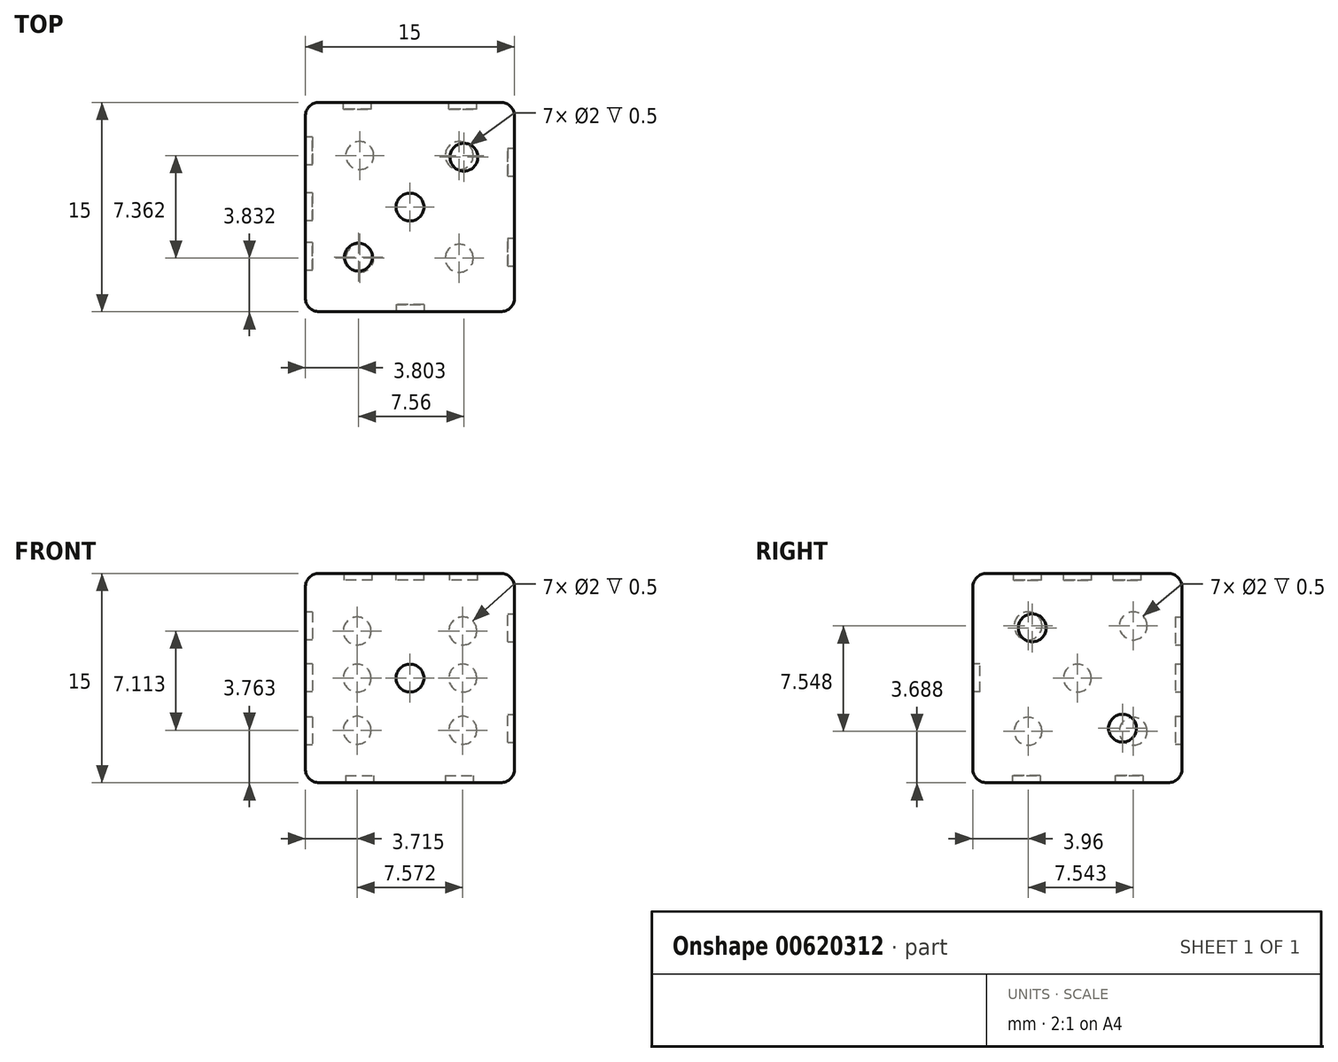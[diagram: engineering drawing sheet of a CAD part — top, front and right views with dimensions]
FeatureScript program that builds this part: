
annotation { "Feature Type Name" : "Feature", "Feature Type Description" : "" }
export const myFeature = defineFeature(function(context is Context, id is Id, definition is map)
    precondition{}
    {
        {
            var Q0;
            Q0=qCreatedBy(makeId("Front.planeOp"),FACE);
            var sketch = newSketch(context, id + "F0", { "sketchPlane" : qUnion([Q0])});
            skLineSegment(sketch, "E0.bottom", {"start": v(7.5, 7.5) * mm, "end": v(-7.5, 7.5) * mm});
            skLineSegment(sketch, "E0.top", {"start": v(7.5, -7.5) * mm, "end": v(-7.5, -7.5) * mm});
            skLineSegment(sketch, "E0.left", {"start": v(7.5, 7.5) * mm, "end": v(7.5, -7.5) * mm});
            skLineSegment(sketch, "E0.right", {"start": v(-7.5, 7.5) * mm, "end": v(-7.5, -7.5) * mm});
            skPoint(sketch, "E0.middle", {"position": v(0, 0) * mm});
            skSolve(sketch);
        }
        {
            var Q0;
            Q0 = qSketchRegion(id + "F0", true);
            extrude(context, id + "F1", {"entities" : qUnion([Q0]), "depth" : 15 * mm, "offsetDistance" : 25.4 * mm});
        }
        {
            var Q0;
            Q0=makeQuery(id+"F1.opExtrude","CAP_FACE",FACE,{"disambiguationData":[OSD([sQuery(id+"F0.wireOp",EDGE,"E0.bottom"),sQuery(id+"F0.wireOp",EDGE,"E0.top"),sQuery(id+"F0.wireOp",EDGE,"E0.left"),sQuery(id+"F0.wireOp",EDGE,"E0.right")])],"isStart":false});
            var sketch = newSketch(context, id + "F2", { "sketchPlane" : qUnion([Q0])});
            skCircle(sketch, "E1", {"center": v(0, 0) * mm, "radius": 1 * mm});
            skSolve(sketch);
        }
        {
            var Q0;
            Q0=makeQuery(id+"F1.opExtrude","CAP_FACE",FACE,{"disambiguationData":[OSD([sQuery(id+"F0.wireOp",EDGE,"E0.bottom"),sQuery(id+"F0.wireOp",EDGE,"E0.top"),sQuery(id+"F0.wireOp",EDGE,"E0.left"),sQuery(id+"F0.wireOp",EDGE,"E0.right")])],"isStart":true});
            var sketch = newSketch(context, id + "F3", { "sketchPlane" : qUnion([Q0])});
            skSolve(sketch);
        }
        {
            var Q0;
            Q0=makeQuery(id+"F2.imprint","IMPRINT",FACE,{"disambiguationData":[TD([[makeQuery(id+"F2.imprint","IMPRINT",EDGE,{"derivedFrom":sQuery(id+"F2.wireOp",EDGE,"E1")}),1.0]])]});
            extrude(context, id + "F4", {"entities" : qUnion([Q0]), "operationType" : NewBodyOperationType.REMOVE, "oppositeDirection" : true, "depth" : 0.5 * mm, "offsetDistance" : 25.4 * mm});
        }
        {
            var Q0;
            Q0=makeQuery(id+"F3.imprint","IMPRINT",FACE,{"disambiguationData":[TD([[makeQuery(id+"F3.imprint","IMPRINT",EDGE,{"derivedFrom":makeQuery(id+"F1.opExtrude","CAP_EDGE",EDGE,{"disambiguationData":[OSD([sQuery(id+"F0.wireOp",EDGE,"E0.bottom")])],"isStart":true})}),-1.0]])]});
            var sketch = newSketch(context, id + "F5", { "sketchPlane" : qUnion([Q0])});
            skLineSegment(sketch, "E2", {"start": v(0, 0) * mm, "end": v(0, -7.54) * mm});
            skPoint(sketch, "E3", {"position": v(-7.48, -3.74) * mm});
            skPoint(sketch, "E4", {"position": v(-3.79, -7.54) * mm});
            skPoint(sketch, "E5", {"position": v(3.79, -7.5) * mm});
            skPoint(sketch, "E6", {"position": v(7.42, -3.74) * mm});
            skPoint(sketch, "E7", {"position": v(-3.79, 7.52) * mm});
            skPoint(sketch, "E8", {"position": v(-7.48, 3.38) * mm});
            skPoint(sketch, "E9", {"position": v(0, 7.52) * mm});
            skPoint(sketch, "E10", {"position": v(3.84, 7.52) * mm});
            skPoint(sketch, "E11", {"position": v(7.31, 3.38) * mm});
            skCircle(sketch, "E12", {"center": v(3.79, -3.74) * mm, "radius": 1 * mm});
            skCircle(sketch, "E13", {"center": v(3.79, 0) * mm, "radius": 1 * mm});
            skCircle(sketch, "E14", {"center": v(3.79, 3.38) * mm, "radius": 1 * mm});
            skCircle(sketch, "E15", {"center": v(-3.79, -3.74) * mm, "radius": 1 * mm});
            skCircle(sketch, "E16", {"center": v(-3.79, 0) * mm, "radius": 1 * mm});
            skCircle(sketch, "E17", {"center": v(-3.79, 3.38) * mm, "radius": 1 * mm});
            skSolve(sketch);
        }
        {
            var Q0;
            Q0 = qSketchRegion(id + "F5", true);
            extrude(context, id + "F6", {"entities" : qUnion([Q0]), "operationType" : NewBodyOperationType.REMOVE, "oppositeDirection" : true, "depth" : 0.5 * mm, "offsetDistance" : 25.4 * mm});
        }
        {
            var Q0;
            Q0=makeQuery(id+"F1.opExtrude","SWEPT_FACE",FACE,{"disambiguationData":[OSD([sQuery(id+"F0.wireOp",EDGE,"E0.top")])]});
            var sketch = newSketch(context, id + "F7", { "sketchPlane" : qUnion([Q0])});
            skPoint(sketch, "E18", {"position": v(-3.6, 0) * mm});
            skPoint(sketch, "E19", {"position": v(-7.5, 7.5) * mm});
            skPoint(sketch, "E20", {"position": v(-7.5, 3.8) * mm});
            skPoint(sketch, "E21", {"position": v(-7.5, 11.17) * mm});
            skPoint(sketch, "E22", {"position": v(-3.6, 15) * mm});
            skPoint(sketch, "E23", {"position": v(7.5, 7.5) * mm});
            skPoint(sketch, "E24", {"position": v(3.53, 0) * mm});
            skPoint(sketch, "E25", {"position": v(7.5, 3.8) * mm});
            skPoint(sketch, "E26", {"position": v(7.5, 11.17) * mm});
            skCircle(sketch, "E27", {"center": v(3.53, 3.8) * mm, "radius": 1 * mm});
            skCircle(sketch, "E28", {"center": v(3.53, 11.17) * mm, "radius": 1 * mm});
            skCircle(sketch, "E29", {"center": v(-3.6, 3.8) * mm, "radius": 1 * mm});
            skCircle(sketch, "E30", {"center": v(-3.6, 11.17) * mm, "radius": 1 * mm});
            skSolve(sketch);
        }
        {
            var Q0;
            Q0 = qSketchRegion(id + "F7", true);
            extrude(context, id + "F8", {"entities" : qUnion([Q0]), "operationType" : NewBodyOperationType.REMOVE, "oppositeDirection" : true, "depth" : 0.5 * mm, "offsetDistance" : 25.4 * mm});
        }
        {
            var Q0;
            Q0=makeQuery(id+"F1.opExtrude","SWEPT_FACE",FACE,{"disambiguationData":[OSD([sQuery(id+"F0.wireOp",EDGE,"E0.right")])]});
            var sketch = newSketch(context, id + "F9", { "sketchPlane" : qUnion([Q0])});
            skPoint(sketch, "E31", {"position": v(0, 0) * mm});
            skPoint(sketch, "E32", {"position": v(3.5, 7.5) * mm});
            skPoint(sketch, "E33", {"position": v(11.04, 7.5) * mm});
            skPoint(sketch, "E34", {"position": v(11.04, -7.5) * mm});
            skPoint(sketch, "E35", {"position": v(3.5, -7.5) * mm});
            skPoint(sketch, "E35.positionSnap0", {"position": v(7.5, -7.5) * mm});
            skPoint(sketch, "E36", {"position": v(0, -3.81) * mm});
            skPoint(sketch, "E37", {"position": v(0, 3.74) * mm});
            skPoint(sketch, "E38", {"position": v(15, 3.74) * mm});
            skPoint(sketch, "E39", {"position": v(15, -3.81) * mm});
            skCircle(sketch, "E40", {"center": v(7.5, 0) * mm, "radius": 1 * mm});
            skCircle(sketch, "E41", {"center": v(3.5, -3.81) * mm, "radius": 1 * mm});
            skCircle(sketch, "E42", {"center": v(11.04, -3.81) * mm, "radius": 1 * mm});
            skCircle(sketch, "E43", {"center": v(11.04, 3.74) * mm, "radius": 1 * mm});
            skCircle(sketch, "E44", {"center": v(3.5, 3.74) * mm, "radius": 1 * mm});
            skSolve(sketch);
        }
        {
            var Q0;
            Q0 = qSketchRegion(id + "F9", true);
            extrude(context, id + "F10", {"entities" : qUnion([Q0]), "operationType" : NewBodyOperationType.REMOVE, "oppositeDirection" : true, "depth" : 0.5 * mm, "offsetDistance" : 25.4 * mm});
        }
        {
            var Q0;
            Q0=makeQuery(id+"F1.opExtrude","SWEPT_FACE",FACE,{"disambiguationData":[OSD([sQuery(id+"F0.wireOp",EDGE,"E0.left")])]});
            var sketch = newSketch(context, id + "F11", { "sketchPlane" : qUnion([Q0])});
            skPoint(sketch, "E45", {"position": v(0, -3.6) * mm});
            skPoint(sketch, "E46", {"position": v(-4.27, -7.5) * mm});
            skPoint(sketch, "E47", {"position": v(-10.73, -7.5) * mm});
            skPoint(sketch, "E48", {"position": v(0, 3.6) * mm});
            skCircle(sketch, "E49", {"center": v(-4.27, -3.6) * mm, "radius": 1 * mm});
            skCircle(sketch, "E50", {"center": v(-10.73, 3.6) * mm, "radius": 1 * mm});
            skSolve(sketch);
        }
        {
            var Q0;
            Q0 = qSketchRegion(id + "F11", true);
            extrude(context, id + "F12", {"entities" : qUnion([Q0]), "operationType" : NewBodyOperationType.REMOVE, "oppositeDirection" : true, "depth" : 0.5 * mm, "offsetDistance" : 25.4 * mm});
        }
        {
            var Q0;
            Q0=makeQuery(id+"F1.opExtrude","SWEPT_FACE",FACE,{"disambiguationData":[OSD([sQuery(id+"F0.wireOp",EDGE,"E0.bottom")])]});
            var sketch = newSketch(context, id + "F13", { "sketchPlane" : qUnion([Q0])});
            skPoint(sketch, "E51", {"position": v(3.86, 0) * mm});
            skPoint(sketch, "E52", {"position": v(7.5, -3.93) * mm});
            skPoint(sketch, "E53", {"position": v(-7.5, -11.09) * mm});
            skPoint(sketch, "E54", {"position": v(-3.7, -15) * mm});
            skCircle(sketch, "E55", {"center": v(3.86, -3.93) * mm, "radius": 1 * mm});
            skCircle(sketch, "E56", {"center": v(0, -7.5) * mm, "radius": 1 * mm});
            skPoint(sketch, "E56.centerSnap0", {"position": v(-7.5, -7.5) * mm});
            skCircle(sketch, "E57", {"center": v(-3.7, -11.09) * mm, "radius": 1 * mm});
            skSolve(sketch);
        }
        {
            var Q0;
            Q0 = qSketchRegion(id + "F13", true);
            extrude(context, id + "F14", {"entities" : qUnion([Q0]), "operationType" : NewBodyOperationType.REMOVE, "oppositeDirection" : true, "depth" : 0.5 * mm, "offsetDistance" : 25.4 * mm});
        }
        {
            var Q0;
            Q0=makeQuery(id+"F1.opExtrude","CAP_EDGE",EDGE,{"disambiguationData":[OSD([sQuery(id+"F0.wireOp",EDGE,"E0.left")])],"isStart":true});
            var Q1;
            Q1=makeQuery(id+"F1.opExtrude","CAP_EDGE",EDGE,{"disambiguationData":[OSD([sQuery(id+"F0.wireOp",EDGE,"E0.top")])],"isStart":true});
            var Q2;
            Q2=makeQuery(id+"F1.opExtrude","SWEPT_EDGE",EDGE,{"disambiguationData":[OSD([sQuery(id+"F0.wireOp",EDGE,"E0.top"),sQuery(id+"F0.wireOp",EDGE,"E0.left")])]});
            var Q3;
            Q3=makeQuery(id+"F1.opExtrude","CAP_EDGE",EDGE,{"disambiguationData":[OSD([sQuery(id+"F0.wireOp",EDGE,"E0.right")])],"isStart":true});
            var Q4;
            Q4=makeQuery(id+"F1.opExtrude","CAP_EDGE",EDGE,{"disambiguationData":[OSD([sQuery(id+"F0.wireOp",EDGE,"E0.bottom")])],"isStart":true});
            var Q5;
            Q5=makeQuery(id+"F1.opExtrude","SWEPT_EDGE",EDGE,{"disambiguationData":[OSD([sQuery(id+"F0.wireOp",EDGE,"E0.bottom"),sQuery(id+"F0.wireOp",EDGE,"E0.right")])]});
            var Q6;
            Q6=makeQuery(id+"F1.opExtrude","SWEPT_EDGE",EDGE,{"disambiguationData":[OSD([sQuery(id+"F0.wireOp",EDGE,"E0.bottom"),sQuery(id+"F0.wireOp",EDGE,"E0.left")])]});
            var Q7;
            Q7=makeQuery(id+"F1.opExtrude","CAP_EDGE",EDGE,{"disambiguationData":[OSD([sQuery(id+"F0.wireOp",EDGE,"E0.bottom")])],"isStart":false});
            var Q8;
            Q8=makeQuery(id+"F1.opExtrude","CAP_EDGE",EDGE,{"disambiguationData":[OSD([sQuery(id+"F0.wireOp",EDGE,"E0.right")])],"isStart":false});
            var Q9;
            Q9=makeQuery(id+"F1.opExtrude","SWEPT_EDGE",EDGE,{"disambiguationData":[OSD([sQuery(id+"F0.wireOp",EDGE,"E0.top"),sQuery(id+"F0.wireOp",EDGE,"E0.right")])]});
            var Q10;
            Q10=makeQuery(id+"F1.opExtrude","CAP_EDGE",EDGE,{"disambiguationData":[OSD([sQuery(id+"F0.wireOp",EDGE,"E0.left")])],"isStart":false});
            var Q11;
            Q11=makeQuery(id+"F1.opExtrude","CAP_EDGE",EDGE,{"disambiguationData":[OSD([sQuery(id+"F0.wireOp",EDGE,"E0.top")])],"isStart":false});
            fillet(context, id + "F15", {"entities" : qUnion([Q0, Q1, Q2, Q3, Q4, Q5, Q6, Q7, Q8, Q9, Q10, Q11]), "radius" : 1 * mm, "tangentPropagation" : true, "allowEdgeOverflow" : false});
        }
    });
